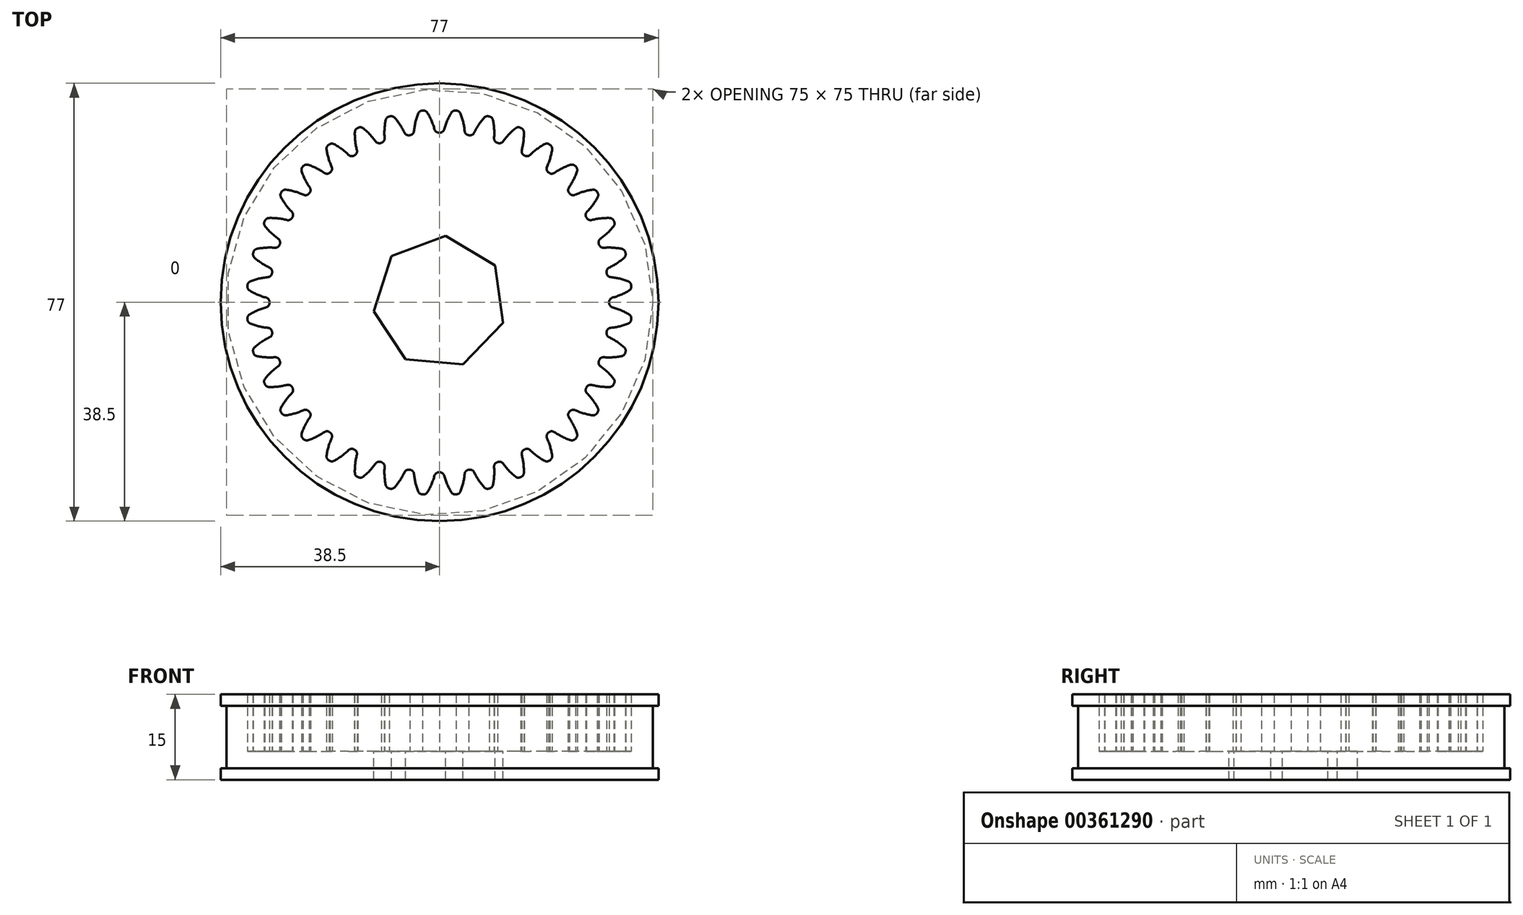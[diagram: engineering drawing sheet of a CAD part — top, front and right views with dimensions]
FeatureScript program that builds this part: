
annotation { "Feature Type Name" : "Feature", "Feature Type Description" : "" }
export const myFeature = defineFeature(function(context is Context, id is Id, definition is map)
    precondition{}
    {
        {
            var Q0;
            Q0=qCreatedBy(makeId("Top.planeOp"),FACE);
            var sketch = newSketch(context, id + "F0", { "sketchPlane" : qUnion([Q0])});
            skCircle(sketch, "E0", {"center": v(-0.05, -0.05) * mm, "radius": 32.1 * mm, "construction": true});
            skCircle(sketch, "E1", {"center": v(-0.05, -0.05) * mm, "radius": 33.88 * mm, "construction": true});
            skCircle(sketch, "E2", {"center": v(-0.05, -0.05) * mm, "radius": 29.88 * mm, "construction": true});
            skLineSegment(sketch, "E3", {"start": v(-0.05, -0.05) * mm, "end": v(-0.05, 34.98) * mm, "construction": true});
            skLineSegment(sketch, "E4", {"start": v(-0.05, -0.05) * mm, "end": v(-6.17, 34.68) * mm, "construction": true});
            skLineSegment(sketch, "E5", {"start": v(-0.05, -0.05) * mm, "end": v(-3.1, 34.94) * mm, "construction": true});
            skCircle(sketch, "E6", {"center": v(-2.84, 31.92) * mm, "radius": 1.4 * mm, "construction": true});
            skPoint(sketch, "E7.center", {"position": v(0, 0) * mm});
            skCircle(sketch, "E8", {"center": v(-2.84, 31.92) * mm, "radius": 10 * mm, "construction": true});
            skArc(sketch, "E9", {"start": v(-1.96, 21.85) * mm, "mid": v(-1.93, 21.91) * mm, "end": v(-1.9, 21.97) * mm});
            skArc(sketch, "E10.trimOffspring", {"start": v(-0.9, 30.41) * mm, "mid": v(-1.42, 31.92) * mm, "end": v(-2.16, 33.33) * mm});
            skLineSegment(sketch, "E11", {"start": v(-2.9, 33.7) * mm, "end": v(-3, 33.7) * mm});
            skLineSegment(sketch, "E12", {"start": v(-0.11, 29.83) * mm, "end": v(-0.05, 29.83) * mm});
            skPoint(sketch, "E13.visualSharp", {"position": v(-0.75, 29.82) * mm});
            skArc(sketch, "E13.filletArc", {"start": v(-0.9, 30.41) * mm, "mid": v(-0.6, 29.99) * mm, "end": v(-0.11, 29.83) * mm});
            skPoint(sketch, "E14.visualSharp", {"position": v(-2.42, 33.74) * mm});
            skArc(sketch, "E14.filletArc", {"start": v(-2.16, 33.33) * mm, "mid": v(-2.47, 33.62) * mm, "end": v(-2.9, 33.7) * mm});
            skArc(sketch, "E15.MirrorCS", {"start": v(-4.5, 30.1) * mm, "mid": v(-4.71, 29.63) * mm, "end": v(-5.17, 29.38) * mm});
            skLineSegment(sketch, "E16.MirrorCS", {"start": v(-5.17, 29.38) * mm, "end": v(-5.23, 29.37) * mm});
            skArc(sketch, "E17.MirrorCS", {"start": v(-4.5, 30.1) * mm, "mid": v(-4.24, 31.67) * mm, "end": v(-3.76, 33.19) * mm});
            skArc(sketch, "E18.MirrorCS", {"start": v(-3.76, 33.19) * mm, "mid": v(-3.5, 33.53) * mm, "end": v(-3.1, 33.7) * mm});
            skLineSegment(sketch, "E19.MirrorCS", {"start": v(-3.1, 33.7) * mm, "end": v(-3, 33.7) * mm});
            skArc(sketch, "E20.1.0", {"start": v(-6.17, 29.8) * mm, "mid": v(-5.81, 29.43) * mm, "end": v(-5.3, 29.36) * mm});
            skLineSegment(sketch, "E20.1.1", {"start": v(-5.3, 29.36) * mm, "end": v(-5.23, 29.37) * mm});
            skArc(sketch, "E20.1.2", {"start": v(-6.17, 29.8) * mm, "mid": v(-6.95, 31.2) * mm, "end": v(-7.92, 32.46) * mm});
            skArc(sketch, "E20.1.3", {"start": v(-7.92, 32.46) * mm, "mid": v(-8.28, 32.7) * mm, "end": v(-8.71, 32.7) * mm});
            skLineSegment(sketch, "E20.1.4", {"start": v(-8.71, 32.7) * mm, "end": v(-8.82, 32.68) * mm});
            skLineSegment(sketch, "E20.1.5", {"start": v(-8.92, 32.65) * mm, "end": v(-8.82, 32.68) * mm});
            skArc(sketch, "E20.1.6", {"start": v(-9.48, 32.04) * mm, "mid": v(-9.28, 32.42) * mm, "end": v(-8.92, 32.65) * mm});
            skArc(sketch, "E20.1.7", {"start": v(-9.67, 28.87) * mm, "mid": v(-9.69, 30.46) * mm, "end": v(-9.48, 32.04) * mm});
            skArc(sketch, "E20.1.8", {"start": v(-9.67, 28.87) * mm, "mid": v(-9.8, 28.37) * mm, "end": v(-10.2, 28.05) * mm});
            skLineSegment(sketch, "E20.1.9", {"start": v(-10.2, 28.05) * mm, "end": v(-10.27, 28.02) * mm});
            skArc(sketch, "E20.2.0", {"start": v(-11.26, 28.29) * mm, "mid": v(-10.84, 27.98) * mm, "end": v(-10.33, 28) * mm});
            skLineSegment(sketch, "E20.2.1", {"start": v(-10.33, 28) * mm, "end": v(-10.27, 28.02) * mm});
            skArc(sketch, "E20.2.2", {"start": v(-11.26, 28.29) * mm, "mid": v(-12.27, 29.52) * mm, "end": v(-13.45, 30.6) * mm});
            skArc(sketch, "E20.2.3", {"start": v(-13.45, 30.6) * mm, "mid": v(-13.84, 30.76) * mm, "end": v(-14.27, 30.7) * mm});
            skLineSegment(sketch, "E20.2.4", {"start": v(-14.27, 30.7) * mm, "end": v(-14.37, 30.66) * mm});
            skLineSegment(sketch, "E20.2.5", {"start": v(-14.46, 30.61) * mm, "end": v(-14.37, 30.66) * mm});
            skArc(sketch, "E20.2.6", {"start": v(-14.91, 29.91) * mm, "mid": v(-14.78, 30.32) * mm, "end": v(-14.46, 30.61) * mm});
            skArc(sketch, "E20.2.7", {"start": v(-14.55, 26.76) * mm, "mid": v(-14.84, 28.32) * mm, "end": v(-14.91, 29.91) * mm});
            skArc(sketch, "E20.2.8", {"start": v(-14.55, 26.76) * mm, "mid": v(-14.58, 26.24) * mm, "end": v(-14.93, 25.86) * mm});
            skLineSegment(sketch, "E20.2.9", {"start": v(-14.93, 25.86) * mm, "end": v(-14.99, 25.82) * mm});
            skArc(sketch, "E20.3.0", {"start": v(-16.01, 25.9) * mm, "mid": v(-15.55, 25.68) * mm, "end": v(-15.04, 25.79) * mm});
            skLineSegment(sketch, "E20.3.1", {"start": v(-15.04, 25.79) * mm, "end": v(-14.99, 25.82) * mm});
            skArc(sketch, "E20.3.2", {"start": v(-16.01, 25.9) * mm, "mid": v(-17.22, 26.95) * mm, "end": v(-18.57, 27.8) * mm});
            skArc(sketch, "E20.3.3", {"start": v(-18.57, 27.8) * mm, "mid": v(-18.99, 27.9) * mm, "end": v(-19.4, 27.76) * mm});
            skLineSegment(sketch, "E20.3.4", {"start": v(-19.4, 27.76) * mm, "end": v(-19.48, 27.7) * mm});
            skLineSegment(sketch, "E20.3.5", {"start": v(-19.57, 27.64) * mm, "end": v(-19.48, 27.7) * mm});
            skArc(sketch, "E20.3.6", {"start": v(-19.89, 26.88) * mm, "mid": v(-19.83, 27.3) * mm, "end": v(-19.57, 27.64) * mm});
            skArc(sketch, "E20.3.7", {"start": v(-18.98, 23.83) * mm, "mid": v(-19.54, 25.32) * mm, "end": v(-19.89, 26.88) * mm});
            skArc(sketch, "E20.3.8", {"start": v(-18.98, 23.83) * mm, "mid": v(-18.93, 23.32) * mm, "end": v(-19.2, 22.88) * mm});
            skLineSegment(sketch, "E20.3.9", {"start": v(-19.2, 22.88) * mm, "end": v(-19.25, 22.84) * mm});
            skArc(sketch, "E20.4.0", {"start": v(-20.28, 22.74) * mm, "mid": v(-19.78, 22.6) * mm, "end": v(-19.3, 22.8) * mm});
            skLineSegment(sketch, "E20.4.1", {"start": v(-19.3, 22.8) * mm, "end": v(-19.25, 22.84) * mm});
            skArc(sketch, "E20.4.2", {"start": v(-20.28, 22.74) * mm, "mid": v(-21.65, 23.55) * mm, "end": v(-23.12, 24.16) * mm});
            skArc(sketch, "E20.4.3", {"start": v(-23.12, 24.16) * mm, "mid": v(-23.55, 24.18) * mm, "end": v(-23.93, 23.98) * mm});
            skLineSegment(sketch, "E20.4.4", {"start": v(-23.93, 23.98) * mm, "end": v(-24, 23.9) * mm});
            skLineSegment(sketch, "E20.4.5", {"start": v(-24.08, 23.83) * mm, "end": v(-24, 23.9) * mm});
            skArc(sketch, "E20.4.6", {"start": v(-24.26, 23.02) * mm, "mid": v(-24.28, 23.45) * mm, "end": v(-24.08, 23.83) * mm});
            skArc(sketch, "E20.4.7", {"start": v(-22.84, 20.18) * mm, "mid": v(-23.65, 21.55) * mm, "end": v(-24.26, 23.02) * mm});
            skArc(sketch, "E20.4.8", {"start": v(-22.84, 20.18) * mm, "mid": v(-22.7, 19.68) * mm, "end": v(-22.9, 19.2) * mm});
            skLineSegment(sketch, "E20.4.9", {"start": v(-22.9, 19.2) * mm, "end": v(-22.94, 19.15) * mm});
            skArc(sketch, "E20.5.0", {"start": v(-23.93, 18.88) * mm, "mid": v(-23.42, 18.83) * mm, "end": v(-22.98, 19.1) * mm});
            skLineSegment(sketch, "E20.5.1", {"start": v(-22.98, 19.1) * mm, "end": v(-22.94, 19.15) * mm});
            skArc(sketch, "E20.5.2", {"start": v(-23.93, 18.88) * mm, "mid": v(-25.42, 19.44) * mm, "end": v(-26.98, 19.79) * mm});
            skArc(sketch, "E20.5.3", {"start": v(-26.98, 19.79) * mm, "mid": v(-27.4, 19.73) * mm, "end": v(-27.74, 19.47) * mm});
            skLineSegment(sketch, "E20.5.4", {"start": v(-27.74, 19.47) * mm, "end": v(-27.8, 19.38) * mm});
            skLineSegment(sketch, "E20.5.5", {"start": v(-27.86, 19.3) * mm, "end": v(-27.8, 19.38) * mm});
            skArc(sketch, "E20.5.6", {"start": v(-27.9, 18.47) * mm, "mid": v(-28, 18.89) * mm, "end": v(-27.86, 19.3) * mm});
            skArc(sketch, "E20.5.7", {"start": v(-26, 15.91) * mm, "mid": v(-27.05, 17.12) * mm, "end": v(-27.9, 18.47) * mm});
            skArc(sketch, "E20.5.8", {"start": v(-26, 15.91) * mm, "mid": v(-25.78, 15.45) * mm, "end": v(-25.89, 14.94) * mm});
            skLineSegment(sketch, "E20.5.9", {"start": v(-25.89, 14.94) * mm, "end": v(-25.92, 14.89) * mm});
            skArc(sketch, "E20.6.0", {"start": v(-26.86, 14.45) * mm, "mid": v(-26.34, 14.48) * mm, "end": v(-25.96, 14.83) * mm});
            skLineSegment(sketch, "E20.6.1", {"start": v(-25.96, 14.83) * mm, "end": v(-25.92, 14.89) * mm});
            skArc(sketch, "E20.6.2", {"start": v(-26.86, 14.45) * mm, "mid": v(-28.42, 14.74) * mm, "end": v(-30.01, 14.81) * mm});
            skArc(sketch, "E20.6.3", {"start": v(-30.01, 14.81) * mm, "mid": v(-30.42, 14.68) * mm, "end": v(-30.71, 14.36) * mm});
            skLineSegment(sketch, "E20.6.4", {"start": v(-30.71, 14.36) * mm, "end": v(-30.76, 14.27) * mm});
            skLineSegment(sketch, "E20.6.5", {"start": v(-30.8, 14.17) * mm, "end": v(-30.76, 14.27) * mm});
            skArc(sketch, "E20.6.6", {"start": v(-30.7, 13.35) * mm, "mid": v(-30.86, 13.74) * mm, "end": v(-30.8, 14.17) * mm});
            skArc(sketch, "E20.6.7", {"start": v(-28.39, 11.16) * mm, "mid": v(-29.62, 12.17) * mm, "end": v(-30.7, 13.35) * mm});
            skArc(sketch, "E20.6.8", {"start": v(-28.39, 11.16) * mm, "mid": v(-28.08, 10.74) * mm, "end": v(-28.1, 10.23) * mm});
            skLineSegment(sketch, "E20.6.9", {"start": v(-28.1, 10.23) * mm, "end": v(-28.12, 10.17) * mm});
            skArc(sketch, "E20.7.0", {"start": v(-28.97, 9.57) * mm, "mid": v(-28.47, 9.7) * mm, "end": v(-28.15, 10.1) * mm});
            skLineSegment(sketch, "E20.7.1", {"start": v(-28.15, 10.1) * mm, "end": v(-28.12, 10.17) * mm});
            skArc(sketch, "E20.7.2", {"start": v(-28.97, 9.57) * mm, "mid": v(-30.56, 9.59) * mm, "end": v(-32.14, 9.38) * mm});
            skArc(sketch, "E20.7.3", {"start": v(-32.14, 9.38) * mm, "mid": v(-32.52, 9.18) * mm, "end": v(-32.75, 8.82) * mm});
            skLineSegment(sketch, "E20.7.4", {"start": v(-32.75, 8.82) * mm, "end": v(-32.78, 8.72) * mm});
            skLineSegment(sketch, "E20.7.5", {"start": v(-32.8, 8.61) * mm, "end": v(-32.78, 8.72) * mm});
            skArc(sketch, "E20.7.6", {"start": v(-32.56, 7.82) * mm, "mid": v(-32.8, 8.18) * mm, "end": v(-32.8, 8.61) * mm});
            skArc(sketch, "E20.7.7", {"start": v(-29.9, 6.07) * mm, "mid": v(-31.3, 6.85) * mm, "end": v(-32.56, 7.82) * mm});
            skArc(sketch, "E20.7.8", {"start": v(-29.9, 6.07) * mm, "mid": v(-29.53, 5.71) * mm, "end": v(-29.46, 5.2) * mm});
            skLineSegment(sketch, "E20.7.9", {"start": v(-29.46, 5.2) * mm, "end": v(-29.47, 5.14) * mm});
            skArc(sketch, "E20.8.0", {"start": v(-30.2, 4.4) * mm, "mid": v(-29.73, 4.62) * mm, "end": v(-29.48, 5.07) * mm});
            skLineSegment(sketch, "E20.8.1", {"start": v(-29.48, 5.07) * mm, "end": v(-29.47, 5.14) * mm});
            skArc(sketch, "E20.8.2", {"start": v(-30.2, 4.4) * mm, "mid": v(-31.77, 4.14) * mm, "end": v(-33.29, 3.66) * mm});
            skArc(sketch, "E20.8.3", {"start": v(-33.29, 3.66) * mm, "mid": v(-33.63, 3.4) * mm, "end": v(-33.8, 3) * mm});
            skLineSegment(sketch, "E20.8.4", {"start": v(-33.8, 3) * mm, "end": v(-33.8, 2.9) * mm});
            skLineSegment(sketch, "E20.8.5", {"start": v(-33.8, 2.8) * mm, "end": v(-33.8, 2.9) * mm});
            skArc(sketch, "E20.8.6", {"start": v(-33.43, 2.06) * mm, "mid": v(-33.72, 2.37) * mm, "end": v(-33.8, 2.8) * mm});
            skArc(sketch, "E20.8.7", {"start": v(-30.51, 0.8) * mm, "mid": v(-32.02, 1.32) * mm, "end": v(-33.43, 2.06) * mm});
            skArc(sketch, "E20.8.8", {"start": v(-30.51, 0.8) * mm, "mid": v(-30.09, 0.5) * mm, "end": v(-29.93, 0.01) * mm});
            skLineSegment(sketch, "E20.8.9", {"start": v(-29.93, 0.01) * mm, "end": v(-29.93, -0.05) * mm});
            skArc(sketch, "E20.9.0", {"start": v(-30.51, -0.9) * mm, "mid": v(-30.09, -0.6) * mm, "end": v(-29.93, -0.12) * mm});
            skLineSegment(sketch, "E20.9.1", {"start": v(-29.93, -0.12) * mm, "end": v(-29.93, -0.05) * mm});
            skArc(sketch, "E20.9.2", {"start": v(-30.51, -0.9) * mm, "mid": v(-32.02, -1.43) * mm, "end": v(-33.43, -2.16) * mm});
            skArc(sketch, "E20.9.3", {"start": v(-33.43, -2.16) * mm, "mid": v(-33.72, -2.48) * mm, "end": v(-33.8, -2.9) * mm});
            skLineSegment(sketch, "E20.9.4", {"start": v(-33.8, -2.9) * mm, "end": v(-33.8, -3) * mm});
            skLineSegment(sketch, "E20.9.5", {"start": v(-33.8, -3.11) * mm, "end": v(-33.8, -3) * mm});
            skArc(sketch, "E20.9.6", {"start": v(-33.29, -3.77) * mm, "mid": v(-33.63, -3.51) * mm, "end": v(-33.8, -3.11) * mm});
            skArc(sketch, "E20.9.7", {"start": v(-30.2, -4.51) * mm, "mid": v(-31.77, -4.25) * mm, "end": v(-33.29, -3.77) * mm});
            skArc(sketch, "E20.9.8", {"start": v(-30.2, -4.51) * mm, "mid": v(-29.73, -4.72) * mm, "end": v(-29.48, -5.18) * mm});
            skLineSegment(sketch, "E20.9.9", {"start": v(-29.48, -5.18) * mm, "end": v(-29.47, -5.24) * mm});
            skArc(sketch, "E20.10.0", {"start": v(-29.9, -6.18) * mm, "mid": v(-29.53, -5.82) * mm, "end": v(-29.46, -5.3) * mm});
            skLineSegment(sketch, "E20.10.1", {"start": v(-29.46, -5.3) * mm, "end": v(-29.47, -5.24) * mm});
            skArc(sketch, "E20.10.2", {"start": v(-29.9, -6.18) * mm, "mid": v(-31.3, -6.96) * mm, "end": v(-32.56, -7.93) * mm});
            skArc(sketch, "E20.10.3", {"start": v(-32.56, -7.93) * mm, "mid": v(-32.8, -8.3) * mm, "end": v(-32.8, -8.72) * mm});
            skLineSegment(sketch, "E20.10.4", {"start": v(-32.8, -8.72) * mm, "end": v(-32.78, -8.82) * mm});
            skLineSegment(sketch, "E20.10.5", {"start": v(-32.75, -8.92) * mm, "end": v(-32.78, -8.82) * mm});
            skArc(sketch, "E20.10.6", {"start": v(-32.14, -9.49) * mm, "mid": v(-32.52, -9.3) * mm, "end": v(-32.75, -8.92) * mm});
            skArc(sketch, "E20.10.7", {"start": v(-28.97, -9.68) * mm, "mid": v(-30.56, -9.7) * mm, "end": v(-32.14, -9.49) * mm});
            skArc(sketch, "E20.10.8", {"start": v(-28.97, -9.68) * mm, "mid": v(-28.47, -9.8) * mm, "end": v(-28.15, -10.21) * mm});
            skLineSegment(sketch, "E20.10.9", {"start": v(-28.15, -10.21) * mm, "end": v(-28.12, -10.27) * mm});
            skArc(sketch, "E20.11.0", {"start": v(-28.39, -11.27) * mm, "mid": v(-28.08, -10.85) * mm, "end": v(-28.1, -10.33) * mm});
            skLineSegment(sketch, "E20.11.1", {"start": v(-28.1, -10.33) * mm, "end": v(-28.12, -10.27) * mm});
            skArc(sketch, "E20.11.2", {"start": v(-28.39, -11.27) * mm, "mid": v(-29.62, -12.28) * mm, "end": v(-30.7, -13.45) * mm});
            skArc(sketch, "E20.11.3", {"start": v(-30.7, -13.45) * mm, "mid": v(-30.86, -13.85) * mm, "end": v(-30.8, -14.28) * mm});
            skLineSegment(sketch, "E20.11.4", {"start": v(-30.8, -14.28) * mm, "end": v(-30.76, -14.37) * mm});
            skLineSegment(sketch, "E20.11.5", {"start": v(-30.71, -14.47) * mm, "end": v(-30.76, -14.37) * mm});
            skArc(sketch, "E20.11.6", {"start": v(-30.01, -14.92) * mm, "mid": v(-30.42, -14.8) * mm, "end": v(-30.71, -14.47) * mm});
            skArc(sketch, "E20.11.7", {"start": v(-26.86, -14.55) * mm, "mid": v(-28.42, -14.85) * mm, "end": v(-30.01, -14.92) * mm});
            skArc(sketch, "E20.11.8", {"start": v(-26.86, -14.55) * mm, "mid": v(-26.34, -14.6) * mm, "end": v(-25.96, -14.94) * mm});
            skLineSegment(sketch, "E20.11.9", {"start": v(-25.96, -14.94) * mm, "end": v(-25.92, -15) * mm});
            skArc(sketch, "E20.12.0", {"start": v(-26, -16.02) * mm, "mid": v(-25.78, -15.56) * mm, "end": v(-25.89, -15.05) * mm});
            skLineSegment(sketch, "E20.12.1", {"start": v(-25.89, -15.05) * mm, "end": v(-25.92, -15) * mm});
            skArc(sketch, "E20.12.2", {"start": v(-26, -16.02) * mm, "mid": v(-27.05, -17.23) * mm, "end": v(-27.9, -18.57) * mm});
            skArc(sketch, "E20.12.3", {"start": v(-27.9, -18.57) * mm, "mid": v(-28, -19) * mm, "end": v(-27.86, -19.4) * mm});
            skLineSegment(sketch, "E20.12.4", {"start": v(-27.86, -19.4) * mm, "end": v(-27.8, -19.49) * mm});
            skLineSegment(sketch, "E20.12.5", {"start": v(-27.74, -19.57) * mm, "end": v(-27.8, -19.49) * mm});
            skArc(sketch, "E20.12.6", {"start": v(-26.98, -19.9) * mm, "mid": v(-27.4, -19.84) * mm, "end": v(-27.74, -19.57) * mm});
            skArc(sketch, "E20.12.7", {"start": v(-23.93, -18.99) * mm, "mid": v(-25.42, -19.55) * mm, "end": v(-26.98, -19.9) * mm});
            skArc(sketch, "E20.12.8", {"start": v(-23.93, -18.99) * mm, "mid": v(-23.42, -18.94) * mm, "end": v(-22.98, -19.2) * mm});
            skLineSegment(sketch, "E20.12.9", {"start": v(-22.98, -19.2) * mm, "end": v(-22.94, -19.26) * mm});
            skArc(sketch, "E20.13.0", {"start": v(-22.84, -20.29) * mm, "mid": v(-22.7, -19.79) * mm, "end": v(-22.9, -19.3) * mm});
            skLineSegment(sketch, "E20.13.1", {"start": v(-22.9, -19.3) * mm, "end": v(-22.94, -19.26) * mm});
            skArc(sketch, "E20.13.2", {"start": v(-22.84, -20.29) * mm, "mid": v(-23.65, -21.66) * mm, "end": v(-24.26, -23.13) * mm});
            skArc(sketch, "E20.13.3", {"start": v(-24.26, -23.13) * mm, "mid": v(-24.28, -23.56) * mm, "end": v(-24.08, -23.94) * mm});
            skLineSegment(sketch, "E20.13.4", {"start": v(-24.08, -23.94) * mm, "end": v(-24, -24.01) * mm});
            skLineSegment(sketch, "E20.13.5", {"start": v(-23.93, -24.09) * mm, "end": v(-24, -24.01) * mm});
            skArc(sketch, "E20.13.6", {"start": v(-23.12, -24.27) * mm, "mid": v(-23.55, -24.3) * mm, "end": v(-23.93, -24.09) * mm});
            skArc(sketch, "E20.13.7", {"start": v(-20.28, -22.85) * mm, "mid": v(-21.65, -23.66) * mm, "end": v(-23.12, -24.27) * mm});
            skArc(sketch, "E20.13.8", {"start": v(-20.28, -22.85) * mm, "mid": v(-19.78, -22.7) * mm, "end": v(-19.3, -22.9) * mm});
            skLineSegment(sketch, "E20.13.9", {"start": v(-19.3, -22.9) * mm, "end": v(-19.25, -22.94) * mm});
            skArc(sketch, "E20.14.0", {"start": v(-18.98, -23.94) * mm, "mid": v(-18.93, -23.42) * mm, "end": v(-19.2, -22.98) * mm});
            skLineSegment(sketch, "E20.14.1", {"start": v(-19.2, -22.98) * mm, "end": v(-19.25, -22.94) * mm});
            skArc(sketch, "E20.14.2", {"start": v(-18.98, -23.94) * mm, "mid": v(-19.54, -25.43) * mm, "end": v(-19.89, -26.98) * mm});
            skArc(sketch, "E20.14.3", {"start": v(-19.89, -26.98) * mm, "mid": v(-19.83, -27.41) * mm, "end": v(-19.57, -27.75) * mm});
            skLineSegment(sketch, "E20.14.4", {"start": v(-19.57, -27.75) * mm, "end": v(-19.48, -27.81) * mm});
            skLineSegment(sketch, "E20.14.5", {"start": v(-19.4, -27.87) * mm, "end": v(-19.48, -27.81) * mm});
            skArc(sketch, "E20.14.6", {"start": v(-18.57, -27.9) * mm, "mid": v(-18.99, -28) * mm, "end": v(-19.4, -27.87) * mm});
            skArc(sketch, "E20.14.7", {"start": v(-16.01, -26.02) * mm, "mid": v(-17.22, -27.05) * mm, "end": v(-18.57, -27.9) * mm});
            skArc(sketch, "E20.14.8", {"start": v(-16.01, -26.02) * mm, "mid": v(-15.55, -25.8) * mm, "end": v(-15.04, -25.9) * mm});
            skLineSegment(sketch, "E20.14.9", {"start": v(-15.04, -25.9) * mm, "end": v(-14.99, -25.93) * mm});
            skArc(sketch, "E20.15.0", {"start": v(-14.55, -26.86) * mm, "mid": v(-14.58, -26.35) * mm, "end": v(-14.93, -25.96) * mm});
            skLineSegment(sketch, "E20.15.1", {"start": v(-14.93, -25.96) * mm, "end": v(-14.99, -25.93) * mm});
            skArc(sketch, "E20.15.2", {"start": v(-14.55, -26.86) * mm, "mid": v(-14.84, -28.43) * mm, "end": v(-14.91, -30.02) * mm});
            skArc(sketch, "E20.15.3", {"start": v(-14.91, -30.02) * mm, "mid": v(-14.78, -30.43) * mm, "end": v(-14.46, -30.72) * mm});
            skLineSegment(sketch, "E20.15.4", {"start": v(-14.46, -30.72) * mm, "end": v(-14.37, -30.76) * mm});
            skLineSegment(sketch, "E20.15.5", {"start": v(-14.27, -30.8) * mm, "end": v(-14.37, -30.76) * mm});
            skArc(sketch, "E20.15.6", {"start": v(-13.45, -30.7) * mm, "mid": v(-13.84, -30.87) * mm, "end": v(-14.27, -30.8) * mm});
            skArc(sketch, "E20.15.7", {"start": v(-11.26, -28.4) * mm, "mid": v(-12.27, -29.63) * mm, "end": v(-13.45, -30.7) * mm});
            skArc(sketch, "E20.15.8", {"start": v(-11.26, -28.4) * mm, "mid": v(-10.84, -28.1) * mm, "end": v(-10.33, -28.1) * mm});
            skLineSegment(sketch, "E20.15.9", {"start": v(-10.33, -28.1) * mm, "end": v(-10.27, -28.13) * mm});
            skArc(sketch, "E20.16.0", {"start": v(-9.67, -28.97) * mm, "mid": v(-9.8, -28.47) * mm, "end": v(-10.2, -28.15) * mm});
            skLineSegment(sketch, "E20.16.1", {"start": v(-10.2, -28.15) * mm, "end": v(-10.27, -28.13) * mm});
            skArc(sketch, "E20.16.2", {"start": v(-9.67, -28.97) * mm, "mid": v(-9.69, -30.57) * mm, "end": v(-9.48, -32.15) * mm});
            skArc(sketch, "E20.16.3", {"start": v(-9.48, -32.15) * mm, "mid": v(-9.28, -32.53) * mm, "end": v(-8.92, -32.75) * mm});
            skLineSegment(sketch, "E20.16.4", {"start": v(-8.92, -32.75) * mm, "end": v(-8.82, -32.78) * mm});
            skLineSegment(sketch, "E20.16.5", {"start": v(-8.71, -32.8) * mm, "end": v(-8.82, -32.78) * mm});
            skArc(sketch, "E20.16.6", {"start": v(-7.92, -32.56) * mm, "mid": v(-8.28, -32.8) * mm, "end": v(-8.71, -32.8) * mm});
            skArc(sketch, "E20.16.7", {"start": v(-6.17, -29.91) * mm, "mid": v(-6.95, -31.3) * mm, "end": v(-7.92, -32.56) * mm});
            skArc(sketch, "E20.16.8", {"start": v(-6.17, -29.91) * mm, "mid": v(-5.81, -29.54) * mm, "end": v(-5.3, -29.47) * mm});
            skLineSegment(sketch, "E20.16.9", {"start": v(-5.3, -29.47) * mm, "end": v(-5.23, -29.48) * mm});
            skArc(sketch, "E20.17.0", {"start": v(-4.5, -30.2) * mm, "mid": v(-4.71, -29.73) * mm, "end": v(-5.17, -29.5) * mm});
            skLineSegment(sketch, "E20.17.1", {"start": v(-5.17, -29.5) * mm, "end": v(-5.23, -29.48) * mm});
            skArc(sketch, "E20.17.2", {"start": v(-4.5, -30.2) * mm, "mid": v(-4.24, -31.78) * mm, "end": v(-3.76, -33.3) * mm});
            skArc(sketch, "E20.17.3", {"start": v(-3.76, -33.3) * mm, "mid": v(-3.5, -33.64) * mm, "end": v(-3.1, -33.8) * mm});
            skLineSegment(sketch, "E20.17.4", {"start": v(-3.1, -33.8) * mm, "end": v(-3, -33.8) * mm});
            skLineSegment(sketch, "E20.17.5", {"start": v(-2.9, -33.82) * mm, "end": v(-3, -33.8) * mm});
            skArc(sketch, "E20.17.6", {"start": v(-2.16, -33.44) * mm, "mid": v(-2.47, -33.73) * mm, "end": v(-2.9, -33.82) * mm});
            skArc(sketch, "E20.17.7", {"start": v(-0.9, -30.52) * mm, "mid": v(-1.42, -32.02) * mm, "end": v(-2.16, -33.44) * mm});
            skArc(sketch, "E20.17.8", {"start": v(-0.9, -30.52) * mm, "mid": v(-0.6, -30.1) * mm, "end": v(-0.11, -29.93) * mm});
            skLineSegment(sketch, "E20.17.9", {"start": v(-0.11, -29.93) * mm, "end": v(-0.05, -29.93) * mm});
            skArc(sketch, "E20.18.0", {"start": v(0.8, -30.52) * mm, "mid": v(0.51, -30.1) * mm, "end": v(0.02, -29.93) * mm});
            skLineSegment(sketch, "E20.18.1", {"start": v(0.02, -29.93) * mm, "end": v(-0.05, -29.93) * mm});
            skArc(sketch, "E20.18.2", {"start": v(0.8, -30.52) * mm, "mid": v(1.33, -32.02) * mm, "end": v(2.06, -33.44) * mm});
            skArc(sketch, "E20.18.3", {"start": v(2.06, -33.44) * mm, "mid": v(2.38, -33.73) * mm, "end": v(2.8, -33.82) * mm});
            skLineSegment(sketch, "E20.18.4", {"start": v(2.8, -33.82) * mm, "end": v(2.9, -33.8) * mm});
            skLineSegment(sketch, "E20.18.5", {"start": v(3.01, -33.8) * mm, "end": v(2.9, -33.8) * mm});
            skArc(sketch, "E20.18.6", {"start": v(3.67, -33.3) * mm, "mid": v(3.41, -33.64) * mm, "end": v(3.01, -33.8) * mm});
            skArc(sketch, "E20.18.7", {"start": v(4.41, -30.2) * mm, "mid": v(4.15, -31.78) * mm, "end": v(3.67, -33.3) * mm});
            skArc(sketch, "E20.18.8", {"start": v(4.41, -30.2) * mm, "mid": v(4.62, -29.73) * mm, "end": v(5.08, -29.5) * mm});
            skLineSegment(sketch, "E20.18.9", {"start": v(5.08, -29.5) * mm, "end": v(5.14, -29.48) * mm});
            skArc(sketch, "E20.19.0", {"start": v(6.08, -29.91) * mm, "mid": v(5.72, -29.54) * mm, "end": v(5.2, -29.47) * mm});
            skLineSegment(sketch, "E20.19.1", {"start": v(5.2, -29.47) * mm, "end": v(5.14, -29.48) * mm});
            skArc(sketch, "E20.19.2", {"start": v(6.08, -29.91) * mm, "mid": v(6.86, -31.3) * mm, "end": v(7.83, -32.56) * mm});
            skArc(sketch, "E20.19.3", {"start": v(7.83, -32.56) * mm, "mid": v(8.2, -32.8) * mm, "end": v(8.62, -32.8) * mm});
            skLineSegment(sketch, "E20.19.4", {"start": v(8.62, -32.8) * mm, "end": v(8.72, -32.78) * mm});
            skLineSegment(sketch, "E20.19.5", {"start": v(8.82, -32.75) * mm, "end": v(8.72, -32.78) * mm});
            skArc(sketch, "E20.19.6", {"start": v(9.39, -32.15) * mm, "mid": v(9.2, -32.53) * mm, "end": v(8.82, -32.75) * mm});
            skArc(sketch, "E20.19.7", {"start": v(9.58, -28.97) * mm, "mid": v(9.6, -30.57) * mm, "end": v(9.39, -32.15) * mm});
            skArc(sketch, "E20.19.8", {"start": v(9.58, -28.97) * mm, "mid": v(9.7, -28.47) * mm, "end": v(10.11, -28.15) * mm});
            skLineSegment(sketch, "E20.19.9", {"start": v(10.11, -28.15) * mm, "end": v(10.17, -28.13) * mm});
            skArc(sketch, "E20.20.0", {"start": v(11.17, -28.4) * mm, "mid": v(10.75, -28.1) * mm, "end": v(10.23, -28.1) * mm});
            skLineSegment(sketch, "E20.20.1", {"start": v(10.23, -28.1) * mm, "end": v(10.17, -28.13) * mm});
            skArc(sketch, "E20.20.2", {"start": v(11.17, -28.4) * mm, "mid": v(12.18, -29.63) * mm, "end": v(13.36, -30.7) * mm});
            skArc(sketch, "E20.20.3", {"start": v(13.36, -30.7) * mm, "mid": v(13.75, -30.87) * mm, "end": v(14.18, -30.8) * mm});
            skLineSegment(sketch, "E20.20.4", {"start": v(14.18, -30.8) * mm, "end": v(14.27, -30.76) * mm});
            skLineSegment(sketch, "E20.20.5", {"start": v(14.37, -30.72) * mm, "end": v(14.27, -30.76) * mm});
            skArc(sketch, "E20.20.6", {"start": v(14.82, -30.02) * mm, "mid": v(14.7, -30.43) * mm, "end": v(14.37, -30.72) * mm});
            skArc(sketch, "E20.20.7", {"start": v(14.45, -26.86) * mm, "mid": v(14.75, -28.43) * mm, "end": v(14.82, -30.02) * mm});
            skArc(sketch, "E20.20.8", {"start": v(14.45, -26.86) * mm, "mid": v(14.5, -26.35) * mm, "end": v(14.84, -25.96) * mm});
            skLineSegment(sketch, "E20.20.9", {"start": v(14.84, -25.96) * mm, "end": v(14.9, -25.93) * mm});
            skArc(sketch, "E20.21.0", {"start": v(15.92, -26.02) * mm, "mid": v(15.46, -25.8) * mm, "end": v(14.95, -25.9) * mm});
            skLineSegment(sketch, "E20.21.1", {"start": v(14.95, -25.9) * mm, "end": v(14.9, -25.93) * mm});
            skArc(sketch, "E20.21.2", {"start": v(15.92, -26.02) * mm, "mid": v(17.13, -27.05) * mm, "end": v(18.47, -27.9) * mm});
            skArc(sketch, "E20.21.3", {"start": v(18.47, -27.9) * mm, "mid": v(18.9, -28) * mm, "end": v(19.3, -27.87) * mm});
            skLineSegment(sketch, "E20.21.4", {"start": v(19.3, -27.87) * mm, "end": v(19.39, -27.81) * mm});
            skLineSegment(sketch, "E20.21.5", {"start": v(19.47, -27.75) * mm, "end": v(19.39, -27.81) * mm});
            skArc(sketch, "E20.21.6", {"start": v(19.8, -26.98) * mm, "mid": v(19.74, -27.41) * mm, "end": v(19.47, -27.75) * mm});
            skArc(sketch, "E20.21.7", {"start": v(18.89, -23.94) * mm, "mid": v(19.45, -25.43) * mm, "end": v(19.8, -26.98) * mm});
            skArc(sketch, "E20.21.8", {"start": v(18.89, -23.94) * mm, "mid": v(18.84, -23.42) * mm, "end": v(19.1, -22.98) * mm});
            skLineSegment(sketch, "E20.21.9", {"start": v(19.1, -22.98) * mm, "end": v(19.16, -22.94) * mm});
            skArc(sketch, "E20.22.0", {"start": v(20.19, -22.85) * mm, "mid": v(19.69, -22.7) * mm, "end": v(19.2, -22.9) * mm});
            skLineSegment(sketch, "E20.22.1", {"start": v(19.2, -22.9) * mm, "end": v(19.16, -22.94) * mm});
            skArc(sketch, "E20.22.2", {"start": v(20.19, -22.85) * mm, "mid": v(21.56, -23.66) * mm, "end": v(23.03, -24.27) * mm});
            skArc(sketch, "E20.22.3", {"start": v(23.03, -24.27) * mm, "mid": v(23.46, -24.3) * mm, "end": v(23.84, -24.09) * mm});
            skLineSegment(sketch, "E20.22.4", {"start": v(23.84, -24.09) * mm, "end": v(23.91, -24.01) * mm});
            skLineSegment(sketch, "E20.22.5", {"start": v(23.99, -23.94) * mm, "end": v(23.91, -24.01) * mm});
            skArc(sketch, "E20.22.6", {"start": v(24.17, -23.13) * mm, "mid": v(24.2, -23.56) * mm, "end": v(23.99, -23.94) * mm});
            skArc(sketch, "E20.22.7", {"start": v(22.75, -20.29) * mm, "mid": v(23.56, -21.66) * mm, "end": v(24.17, -23.13) * mm});
            skArc(sketch, "E20.22.8", {"start": v(22.75, -20.29) * mm, "mid": v(22.6, -19.79) * mm, "end": v(22.8, -19.3) * mm});
            skLineSegment(sketch, "E20.22.9", {"start": v(22.8, -19.3) * mm, "end": v(22.84, -19.26) * mm});
            skArc(sketch, "E20.23.0", {"start": v(23.84, -18.99) * mm, "mid": v(23.32, -18.94) * mm, "end": v(22.88, -19.2) * mm});
            skLineSegment(sketch, "E20.23.1", {"start": v(22.88, -19.2) * mm, "end": v(22.84, -19.26) * mm});
            skArc(sketch, "E20.23.2", {"start": v(23.84, -18.99) * mm, "mid": v(25.33, -19.55) * mm, "end": v(26.88, -19.9) * mm});
            skArc(sketch, "E20.23.3", {"start": v(26.88, -19.9) * mm, "mid": v(27.31, -19.84) * mm, "end": v(27.65, -19.57) * mm});
            skLineSegment(sketch, "E20.23.4", {"start": v(27.65, -19.57) * mm, "end": v(27.71, -19.49) * mm});
            skLineSegment(sketch, "E20.23.5", {"start": v(27.77, -19.4) * mm, "end": v(27.71, -19.49) * mm});
            skArc(sketch, "E20.23.6", {"start": v(27.8, -18.57) * mm, "mid": v(27.9, -19) * mm, "end": v(27.77, -19.4) * mm});
            skArc(sketch, "E20.23.7", {"start": v(25.92, -16.02) * mm, "mid": v(26.95, -17.23) * mm, "end": v(27.8, -18.57) * mm});
            skArc(sketch, "E20.23.8", {"start": v(25.92, -16.02) * mm, "mid": v(25.7, -15.56) * mm, "end": v(25.8, -15.05) * mm});
            skLineSegment(sketch, "E20.23.9", {"start": v(25.8, -15.05) * mm, "end": v(25.83, -15) * mm});
            skArc(sketch, "E20.24.0", {"start": v(26.76, -14.55) * mm, "mid": v(26.25, -14.6) * mm, "end": v(25.86, -14.94) * mm});
            skLineSegment(sketch, "E20.24.1", {"start": v(25.86, -14.94) * mm, "end": v(25.83, -15) * mm});
            skArc(sketch, "E20.24.2", {"start": v(26.76, -14.55) * mm, "mid": v(28.33, -14.85) * mm, "end": v(29.92, -14.92) * mm});
            skArc(sketch, "E20.24.3", {"start": v(29.92, -14.92) * mm, "mid": v(30.33, -14.8) * mm, "end": v(30.62, -14.47) * mm});
            skLineSegment(sketch, "E20.24.4", {"start": v(30.62, -14.47) * mm, "end": v(30.66, -14.37) * mm});
            skLineSegment(sketch, "E20.24.5", {"start": v(30.7, -14.28) * mm, "end": v(30.66, -14.37) * mm});
            skArc(sketch, "E20.24.6", {"start": v(30.6, -13.45) * mm, "mid": v(30.77, -13.85) * mm, "end": v(30.7, -14.28) * mm});
            skArc(sketch, "E20.24.7", {"start": v(28.3, -11.27) * mm, "mid": v(29.53, -12.28) * mm, "end": v(30.6, -13.45) * mm});
            skArc(sketch, "E20.24.8", {"start": v(28.3, -11.27) * mm, "mid": v(28, -10.85) * mm, "end": v(28, -10.33) * mm});
            skLineSegment(sketch, "E20.24.9", {"start": v(28, -10.33) * mm, "end": v(28.03, -10.27) * mm});
            skArc(sketch, "E20.25.0", {"start": v(28.87, -9.68) * mm, "mid": v(28.37, -9.8) * mm, "end": v(28.05, -10.21) * mm});
            skLineSegment(sketch, "E20.25.1", {"start": v(28.05, -10.21) * mm, "end": v(28.03, -10.27) * mm});
            skArc(sketch, "E20.25.2", {"start": v(28.87, -9.68) * mm, "mid": v(30.47, -9.7) * mm, "end": v(32.05, -9.49) * mm});
            skArc(sketch, "E20.25.3", {"start": v(32.05, -9.49) * mm, "mid": v(32.43, -9.3) * mm, "end": v(32.66, -8.92) * mm});
            skLineSegment(sketch, "E20.25.4", {"start": v(32.66, -8.92) * mm, "end": v(32.68, -8.82) * mm});
            skLineSegment(sketch, "E20.25.5", {"start": v(32.7, -8.72) * mm, "end": v(32.68, -8.82) * mm});
            skArc(sketch, "E20.25.6", {"start": v(32.46, -7.93) * mm, "mid": v(32.7, -8.3) * mm, "end": v(32.7, -8.72) * mm});
            skArc(sketch, "E20.25.7", {"start": v(29.81, -6.18) * mm, "mid": v(31.2, -6.96) * mm, "end": v(32.46, -7.93) * mm});
            skArc(sketch, "E20.25.8", {"start": v(29.81, -6.18) * mm, "mid": v(29.44, -5.82) * mm, "end": v(29.37, -5.3) * mm});
            skLineSegment(sketch, "E20.25.9", {"start": v(29.37, -5.3) * mm, "end": v(29.38, -5.24) * mm});
            skArc(sketch, "E20.26.0", {"start": v(30.1, -4.51) * mm, "mid": v(29.63, -4.72) * mm, "end": v(29.4, -5.18) * mm});
            skLineSegment(sketch, "E20.26.1", {"start": v(29.4, -5.18) * mm, "end": v(29.38, -5.24) * mm});
            skArc(sketch, "E20.26.2", {"start": v(30.1, -4.51) * mm, "mid": v(31.68, -4.25) * mm, "end": v(33.2, -3.77) * mm});
            skArc(sketch, "E20.26.3", {"start": v(33.2, -3.77) * mm, "mid": v(33.54, -3.51) * mm, "end": v(33.7, -3.11) * mm});
            skLineSegment(sketch, "E20.26.4", {"start": v(33.7, -3.11) * mm, "end": v(33.7, -3) * mm});
            skLineSegment(sketch, "E20.26.5", {"start": v(33.72, -2.9) * mm, "end": v(33.7, -3) * mm});
            skArc(sketch, "E20.26.6", {"start": v(33.34, -2.16) * mm, "mid": v(33.63, -2.48) * mm, "end": v(33.72, -2.9) * mm});
            skArc(sketch, "E20.26.7", {"start": v(30.42, -0.9) * mm, "mid": v(31.92, -1.43) * mm, "end": v(33.34, -2.16) * mm});
            skArc(sketch, "E20.26.8", {"start": v(30.42, -0.9) * mm, "mid": v(30, -0.6) * mm, "end": v(29.83, -0.12) * mm});
            skLineSegment(sketch, "E20.26.9", {"start": v(29.83, -0.12) * mm, "end": v(29.83, -0.05) * mm});
            skArc(sketch, "E20.27.0", {"start": v(30.42, 0.8) * mm, "mid": v(30, 0.5) * mm, "end": v(29.83, 0.01) * mm});
            skLineSegment(sketch, "E20.27.1", {"start": v(29.83, 0.01) * mm, "end": v(29.83, -0.05) * mm});
            skArc(sketch, "E20.27.2", {"start": v(30.42, 0.8) * mm, "mid": v(31.92, 1.32) * mm, "end": v(33.34, 2.06) * mm});
            skArc(sketch, "E20.27.3", {"start": v(33.34, 2.06) * mm, "mid": v(33.63, 2.37) * mm, "end": v(33.72, 2.8) * mm});
            skLineSegment(sketch, "E20.27.4", {"start": v(33.72, 2.8) * mm, "end": v(33.7, 2.9) * mm});
            skLineSegment(sketch, "E20.27.5", {"start": v(33.7, 3) * mm, "end": v(33.7, 2.9) * mm});
            skArc(sketch, "E20.27.6", {"start": v(33.2, 3.66) * mm, "mid": v(33.54, 3.4) * mm, "end": v(33.7, 3) * mm});
            skArc(sketch, "E20.27.7", {"start": v(30.1, 4.4) * mm, "mid": v(31.68, 4.14) * mm, "end": v(33.2, 3.66) * mm});
            skArc(sketch, "E20.27.8", {"start": v(30.1, 4.4) * mm, "mid": v(29.63, 4.62) * mm, "end": v(29.4, 5.07) * mm});
            skLineSegment(sketch, "E20.27.9", {"start": v(29.4, 5.07) * mm, "end": v(29.38, 5.14) * mm});
            skArc(sketch, "E20.28.0", {"start": v(29.81, 6.07) * mm, "mid": v(29.44, 5.71) * mm, "end": v(29.37, 5.2) * mm});
            skLineSegment(sketch, "E20.28.1", {"start": v(29.37, 5.2) * mm, "end": v(29.38, 5.14) * mm});
            skArc(sketch, "E20.28.2", {"start": v(29.81, 6.07) * mm, "mid": v(31.2, 6.85) * mm, "end": v(32.46, 7.82) * mm});
            skArc(sketch, "E20.28.3", {"start": v(32.46, 7.82) * mm, "mid": v(32.7, 8.18) * mm, "end": v(32.7, 8.61) * mm});
            skLineSegment(sketch, "E20.28.4", {"start": v(32.7, 8.61) * mm, "end": v(32.68, 8.72) * mm});
            skLineSegment(sketch, "E20.28.5", {"start": v(32.66, 8.82) * mm, "end": v(32.68, 8.72) * mm});
            skArc(sketch, "E20.28.6", {"start": v(32.05, 9.38) * mm, "mid": v(32.43, 9.18) * mm, "end": v(32.66, 8.82) * mm});
            skArc(sketch, "E20.28.7", {"start": v(28.87, 9.57) * mm, "mid": v(30.47, 9.59) * mm, "end": v(32.05, 9.38) * mm});
            skArc(sketch, "E20.28.8", {"start": v(28.87, 9.57) * mm, "mid": v(28.37, 9.7) * mm, "end": v(28.05, 10.1) * mm});
            skLineSegment(sketch, "E20.28.9", {"start": v(28.05, 10.1) * mm, "end": v(28.03, 10.17) * mm});
            skArc(sketch, "E20.29.0", {"start": v(28.3, 11.16) * mm, "mid": v(28, 10.74) * mm, "end": v(28, 10.23) * mm});
            skLineSegment(sketch, "E20.29.1", {"start": v(28, 10.23) * mm, "end": v(28.03, 10.17) * mm});
            skArc(sketch, "E20.29.2", {"start": v(28.3, 11.16) * mm, "mid": v(29.53, 12.17) * mm, "end": v(30.6, 13.35) * mm});
            skArc(sketch, "E20.29.3", {"start": v(30.6, 13.35) * mm, "mid": v(30.77, 13.74) * mm, "end": v(30.7, 14.17) * mm});
            skLineSegment(sketch, "E20.29.4", {"start": v(30.7, 14.17) * mm, "end": v(30.66, 14.27) * mm});
            skLineSegment(sketch, "E20.29.5", {"start": v(30.62, 14.36) * mm, "end": v(30.66, 14.27) * mm});
            skArc(sketch, "E20.29.6", {"start": v(29.92, 14.81) * mm, "mid": v(30.33, 14.68) * mm, "end": v(30.62, 14.36) * mm});
            skArc(sketch, "E20.29.7", {"start": v(26.76, 14.45) * mm, "mid": v(28.33, 14.74) * mm, "end": v(29.92, 14.81) * mm});
            skArc(sketch, "E20.29.8", {"start": v(26.76, 14.45) * mm, "mid": v(26.25, 14.48) * mm, "end": v(25.86, 14.83) * mm});
            skLineSegment(sketch, "E20.29.9", {"start": v(25.86, 14.83) * mm, "end": v(25.83, 14.89) * mm});
            skArc(sketch, "E20.30.0", {"start": v(25.92, 15.91) * mm, "mid": v(25.7, 15.45) * mm, "end": v(25.8, 14.94) * mm});
            skLineSegment(sketch, "E20.30.1", {"start": v(25.8, 14.94) * mm, "end": v(25.83, 14.89) * mm});
            skArc(sketch, "E20.30.2", {"start": v(25.92, 15.91) * mm, "mid": v(26.95, 17.12) * mm, "end": v(27.8, 18.47) * mm});
            skArc(sketch, "E20.30.3", {"start": v(27.8, 18.47) * mm, "mid": v(27.9, 18.89) * mm, "end": v(27.77, 19.3) * mm});
            skLineSegment(sketch, "E20.30.4", {"start": v(27.77, 19.3) * mm, "end": v(27.71, 19.38) * mm});
            skLineSegment(sketch, "E20.30.5", {"start": v(27.65, 19.47) * mm, "end": v(27.71, 19.38) * mm});
            skArc(sketch, "E20.30.6", {"start": v(26.88, 19.79) * mm, "mid": v(27.31, 19.73) * mm, "end": v(27.65, 19.47) * mm});
            skArc(sketch, "E20.30.7", {"start": v(23.84, 18.88) * mm, "mid": v(25.33, 19.44) * mm, "end": v(26.88, 19.79) * mm});
            skArc(sketch, "E20.30.8", {"start": v(23.84, 18.88) * mm, "mid": v(23.32, 18.83) * mm, "end": v(22.88, 19.1) * mm});
            skLineSegment(sketch, "E20.30.9", {"start": v(22.88, 19.1) * mm, "end": v(22.84, 19.15) * mm});
            skArc(sketch, "E20.31.0", {"start": v(22.75, 20.18) * mm, "mid": v(22.6, 19.68) * mm, "end": v(22.8, 19.2) * mm});
            skLineSegment(sketch, "E20.31.1", {"start": v(22.8, 19.2) * mm, "end": v(22.84, 19.15) * mm});
            skArc(sketch, "E20.31.2", {"start": v(22.75, 20.18) * mm, "mid": v(23.56, 21.55) * mm, "end": v(24.17, 23.02) * mm});
            skArc(sketch, "E20.31.3", {"start": v(24.17, 23.02) * mm, "mid": v(24.2, 23.45) * mm, "end": v(23.99, 23.83) * mm});
            skLineSegment(sketch, "E20.31.4", {"start": v(23.99, 23.83) * mm, "end": v(23.91, 23.9) * mm});
            skLineSegment(sketch, "E20.31.5", {"start": v(23.84, 23.98) * mm, "end": v(23.91, 23.9) * mm});
            skArc(sketch, "E20.31.6", {"start": v(23.03, 24.16) * mm, "mid": v(23.46, 24.18) * mm, "end": v(23.84, 23.98) * mm});
            skArc(sketch, "E20.31.7", {"start": v(20.19, 22.74) * mm, "mid": v(21.56, 23.55) * mm, "end": v(23.03, 24.16) * mm});
            skArc(sketch, "E20.31.8", {"start": v(20.19, 22.74) * mm, "mid": v(19.69, 22.6) * mm, "end": v(19.2, 22.8) * mm});
            skLineSegment(sketch, "E20.31.9", {"start": v(19.2, 22.8) * mm, "end": v(19.16, 22.84) * mm});
            skArc(sketch, "E20.32.0", {"start": v(18.89, 23.83) * mm, "mid": v(18.84, 23.32) * mm, "end": v(19.1, 22.88) * mm});
            skLineSegment(sketch, "E20.32.1", {"start": v(19.1, 22.88) * mm, "end": v(19.16, 22.84) * mm});
            skArc(sketch, "E20.32.2", {"start": v(18.89, 23.83) * mm, "mid": v(19.45, 25.32) * mm, "end": v(19.8, 26.88) * mm});
            skArc(sketch, "E20.32.3", {"start": v(19.8, 26.88) * mm, "mid": v(19.74, 27.3) * mm, "end": v(19.47, 27.64) * mm});
            skLineSegment(sketch, "E20.32.4", {"start": v(19.47, 27.64) * mm, "end": v(19.39, 27.7) * mm});
            skLineSegment(sketch, "E20.32.5", {"start": v(19.3, 27.76) * mm, "end": v(19.39, 27.7) * mm});
            skArc(sketch, "E20.32.6", {"start": v(18.47, 27.8) * mm, "mid": v(18.9, 27.9) * mm, "end": v(19.3, 27.76) * mm});
            skArc(sketch, "E20.32.7", {"start": v(15.92, 25.9) * mm, "mid": v(17.13, 26.95) * mm, "end": v(18.47, 27.8) * mm});
            skArc(sketch, "E20.32.8", {"start": v(15.92, 25.9) * mm, "mid": v(15.46, 25.68) * mm, "end": v(14.95, 25.79) * mm});
            skLineSegment(sketch, "E20.32.9", {"start": v(14.95, 25.79) * mm, "end": v(14.9, 25.82) * mm});
            skArc(sketch, "E20.33.0", {"start": v(14.45, 26.76) * mm, "mid": v(14.5, 26.24) * mm, "end": v(14.84, 25.86) * mm});
            skLineSegment(sketch, "E20.33.1", {"start": v(14.84, 25.86) * mm, "end": v(14.9, 25.82) * mm});
            skArc(sketch, "E20.33.2", {"start": v(14.45, 26.76) * mm, "mid": v(14.75, 28.32) * mm, "end": v(14.82, 29.91) * mm});
            skArc(sketch, "E20.33.3", {"start": v(14.82, 29.91) * mm, "mid": v(14.7, 30.32) * mm, "end": v(14.37, 30.61) * mm});
            skLineSegment(sketch, "E20.33.4", {"start": v(14.37, 30.61) * mm, "end": v(14.27, 30.66) * mm});
            skLineSegment(sketch, "E20.33.5", {"start": v(14.18, 30.7) * mm, "end": v(14.27, 30.66) * mm});
            skArc(sketch, "E20.33.6", {"start": v(13.36, 30.6) * mm, "mid": v(13.75, 30.76) * mm, "end": v(14.18, 30.7) * mm});
            skArc(sketch, "E20.33.7", {"start": v(11.17, 28.29) * mm, "mid": v(12.18, 29.52) * mm, "end": v(13.36, 30.6) * mm});
            skArc(sketch, "E20.33.8", {"start": v(11.17, 28.29) * mm, "mid": v(10.75, 27.98) * mm, "end": v(10.23, 28) * mm});
            skLineSegment(sketch, "E20.33.9", {"start": v(10.23, 28) * mm, "end": v(10.17, 28.02) * mm});
            skArc(sketch, "E20.34.0", {"start": v(9.58, 28.87) * mm, "mid": v(9.7, 28.37) * mm, "end": v(10.11, 28.05) * mm});
            skLineSegment(sketch, "E20.34.1", {"start": v(10.11, 28.05) * mm, "end": v(10.17, 28.02) * mm});
            skArc(sketch, "E20.34.2", {"start": v(9.58, 28.87) * mm, "mid": v(9.6, 30.46) * mm, "end": v(9.39, 32.04) * mm});
            skArc(sketch, "E20.34.3", {"start": v(9.39, 32.04) * mm, "mid": v(9.2, 32.42) * mm, "end": v(8.82, 32.65) * mm});
            skLineSegment(sketch, "E20.34.4", {"start": v(8.82, 32.65) * mm, "end": v(8.72, 32.68) * mm});
            skLineSegment(sketch, "E20.34.5", {"start": v(8.62, 32.7) * mm, "end": v(8.72, 32.68) * mm});
            skArc(sketch, "E20.34.6", {"start": v(7.83, 32.46) * mm, "mid": v(8.2, 32.7) * mm, "end": v(8.62, 32.7) * mm});
            skArc(sketch, "E20.34.7", {"start": v(6.08, 29.8) * mm, "mid": v(6.86, 31.2) * mm, "end": v(7.83, 32.46) * mm});
            skArc(sketch, "E20.34.8", {"start": v(6.08, 29.8) * mm, "mid": v(5.72, 29.43) * mm, "end": v(5.2, 29.36) * mm});
            skLineSegment(sketch, "E20.34.9", {"start": v(5.2, 29.36) * mm, "end": v(5.14, 29.37) * mm});
            skArc(sketch, "E20.35.0", {"start": v(4.41, 30.1) * mm, "mid": v(4.62, 29.63) * mm, "end": v(5.08, 29.38) * mm});
            skLineSegment(sketch, "E20.35.1", {"start": v(5.08, 29.38) * mm, "end": v(5.14, 29.37) * mm});
            skArc(sketch, "E20.35.2", {"start": v(4.41, 30.1) * mm, "mid": v(4.15, 31.67) * mm, "end": v(3.67, 33.19) * mm});
            skArc(sketch, "E20.35.3", {"start": v(3.67, 33.19) * mm, "mid": v(3.41, 33.53) * mm, "end": v(3.01, 33.7) * mm});
            skLineSegment(sketch, "E20.35.4", {"start": v(3.01, 33.7) * mm, "end": v(2.9, 33.7) * mm});
            skLineSegment(sketch, "E20.35.5", {"start": v(2.8, 33.7) * mm, "end": v(2.9, 33.7) * mm});
            skArc(sketch, "E20.35.6", {"start": v(2.06, 33.33) * mm, "mid": v(2.38, 33.62) * mm, "end": v(2.8, 33.7) * mm});
            skArc(sketch, "E20.35.7", {"start": v(0.8, 30.41) * mm, "mid": v(1.33, 31.92) * mm, "end": v(2.06, 33.33) * mm});
            skArc(sketch, "E20.35.8", {"start": v(0.8, 30.41) * mm, "mid": v(0.51, 29.99) * mm, "end": v(0.02, 29.83) * mm});
            skLineSegment(sketch, "E20.35.9", {"start": v(0.02, 29.83) * mm, "end": v(-0.05, 29.83) * mm});
            skCircle(sketch, "E21.cCircle", {"center": v(0, 0) * mm, "radius": 10.55 * mm, "construction": true});
            skLineSegment(sketch, "E21.0", {"start": v(11.14, -3.61) * mm, "end": v(4.12, -10.96) * mm});
            skLineSegment(sketch, "E21.1", {"start": v(4.12, -10.96) * mm, "end": v(-6, -10.06) * mm});
            skLineSegment(sketch, "E21.2", {"start": v(-6, -10.06) * mm, "end": v(-11.6, -1.58) * mm});
            skLineSegment(sketch, "E21.3", {"start": v(-11.6, -1.58) * mm, "end": v(-8.47, 8.09) * mm});
            skLineSegment(sketch, "E21.4", {"start": v(-8.47, 8.09) * mm, "end": v(1.04, 11.66) * mm});
            skLineSegment(sketch, "E21.5", {"start": v(1.04, 11.66) * mm, "end": v(9.77, 6.46) * mm});
            skLineSegment(sketch, "E21.6", {"start": v(9.77, 6.46) * mm, "end": v(11.14, -3.61) * mm});
            skPoint(sketch, "E21.0.midPoint", {"position": v(7.63, -7.29) * mm});
            skCircle(sketch, "E22", {"center": v(0, 0) * mm, "radius": 37.5 * mm});
            skSolve(sketch);
        }
        {
            var Q0;
            Q0=makeQuery(id+"F0.imprint","IMPRINT",FACE,{"disambiguationData":[TD([[makeQuery(id+"F0.imprint","IMPRINT",EDGE,{"derivedFrom":sQuery(id+"F0.wireOp",EDGE,"E10.trimOffspring")}),-1.0]])]});
            extrude(context, id + "F1", {"entities" : qUnion([Q0]), "depth" : 10 * mm});
        }
        {
            var Q0;
            Q0=makeQuery(id+"F0.imprint","IMPRINT",FACE,{"disambiguationData":[TD([[makeQuery(id+"F0.imprint","IMPRINT",EDGE,{"derivedFrom":sQuery(id+"F0.wireOp",EDGE,"E10.trimOffspring")}),-1.0]])]});
            var Q1;
            Q1=makeQuery(id+"F0.imprint","IMPRINT",FACE,{"disambiguationData":[TD([[makeQuery(id+"F0.imprint","IMPRINT",EDGE,{"derivedFrom":sQuery(id+"F0.wireOp",EDGE,"E10.trimOffspring")}),1.0]])]});
            extrude(context, id + "F2", {"entities" : qUnion([Q0, Q1]), "operationType" : NewBodyOperationType.ADD, "oppositeDirection" : true, "depth" : 5 * mm});
        }
        {
            var Q0;
            Q0=qCreatedBy(makeId("Front.planeOp"),FACE);
            var sketch = newSketch(context, id + "F3", { "sketchPlane" : qUnion([Q0])});
            skLineSegment(sketch, "E23", {"start": v(0, 0) * mm, "end": v(37.5, 0) * mm, "construction": true});
            skLineSegment(sketch, "E24", {"start": v(0, 19.6) * mm, "end": v(0, -19.45) * mm, "construction": true});
            skLineSegment(sketch, "E25", {"start": v(37.5, 0) * mm, "end": v(37.5, -6.63) * mm, "construction": true});
            skLineSegment(sketch, "E26", {"start": v(37.5, 0) * mm, "end": v(37.5, 11.05) * mm, "construction": true});
            skLineSegment(sketch, "E27", {"start": v(37.5, -5) * mm, "end": v(38.5, -5) * mm});
            skLineSegment(sketch, "E28", {"start": v(38.5, -5) * mm, "end": v(38.5, -3) * mm});
            skLineSegment(sketch, "E29", {"start": v(38.5, -3) * mm, "end": v(37.5, -3) * mm});
            skLineSegment(sketch, "E30", {"start": v(37.5, 10) * mm, "end": v(38.5, 10) * mm});
            skLineSegment(sketch, "E31", {"start": v(38.5, 10) * mm, "end": v(38.5, 8) * mm});
            skLineSegment(sketch, "E32", {"start": v(38.5, 8) * mm, "end": v(37.5, 8) * mm});
            skLineSegment(sketch, "E33", {"start": v(37.5, 10) * mm, "end": v(37.5, 8) * mm});
            skLineSegment(sketch, "E34", {"start": v(37.5, -3) * mm, "end": v(37.5, -5) * mm});
            skSolve(sketch);
        }
        {
            var Q0;
            Q0=makeQuery(id+"F3.imprint","IMPRINT",FACE,{"disambiguationData":[TD([[makeQuery(id+"F3.imprint","IMPRINT",EDGE,{"derivedFrom":sQuery(id+"F3.wireOp",EDGE,"E30")}),-1.0]])]});
            var Q1;
            Q1=makeQuery(id+"F3.imprint","IMPRINT",FACE,{"disambiguationData":[TD([[makeQuery(id+"F3.imprint","IMPRINT",EDGE,{"derivedFrom":sQuery(id+"F3.wireOp",EDGE,"E27")}),1.0]])]});
            var Q2;
            Q2=sQuery(id+"F3.wireOp",EDGE,"E24");
            revolve(context, id + "F4", {"operationType" : NewBodyOperationType.ADD, "entities" : qUnion([Q0, Q1]), "axis" : qUnion([Q2]), "revolveType" : RevolveType.FULL});
        }
    });
